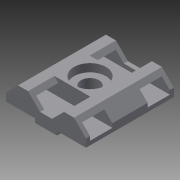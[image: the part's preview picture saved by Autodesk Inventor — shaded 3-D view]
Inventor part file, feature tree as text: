
AUTODESK INVENTOR PART (.ipt)
format: ipt  version: 2015 SP1 (Build 190203100, 203)  size: 177,152 bytes
history: native  units: mm
features: extrude x5, sketch x4, chamfer x2, hole x1
ambient origin geometry x8: Origin, YZ Plane, XZ Plane, XY Plane, X Axis, Y Axis, Z Axis, Center Point
bodies: Solid1 (feature_tree)
feature tree (12):
  extrude  "Extrusion1"  Depth=22.0mm
  chamfer  "Chamfer7"  Distance=5.0mm
  extrude  "Extrusion2"  Depth=1.0mm TaperAngle=0.0deg
  extrude  "Extrusion3"  Depth=5.5mm
  extrude  "Extrusion7"  Depth=3.0mm
  chamfer  "Chamfer8"  Distance=3.0mm
  extrude  "Extrusion8"  Depth=3.0mm
  hole  "Hole2"  [1 undecoded]
  sketch  "Sketch1"  dims[d0=20.0mm d1=22.0mm d3=5.0mm d4=0.0mm]
  sketch  "Sketch2"  dims[d5=5.5mm d6=1.0mm d7=0.0mm]
  sketch  "Sketch3"  dims[d8=5.5mm d9=5.5mm]
  sketch  "Sketch10"  dims[d10=1.0mm d11=0.0mm d60=3.0mm d61=2.0mm d62=22.68928mm d64=3.0mm d65=0.0mm d66=3.0mm d67=2.0mm d68=22.68928mm d73=3.0mm d74=0.0mm d75=4.5mm d76=6.0mm d77=8.0mm d78=2.0mm d79=90.0deg d80=8.0mm d81=20.594885mm d83=3.0mm d85=1.0mm]
note: 1 required parameter value undecoded (feature->parameter linkage not recoverable at this tier; creation-order binding heuristic only, values carry confidence <= 0.55)
